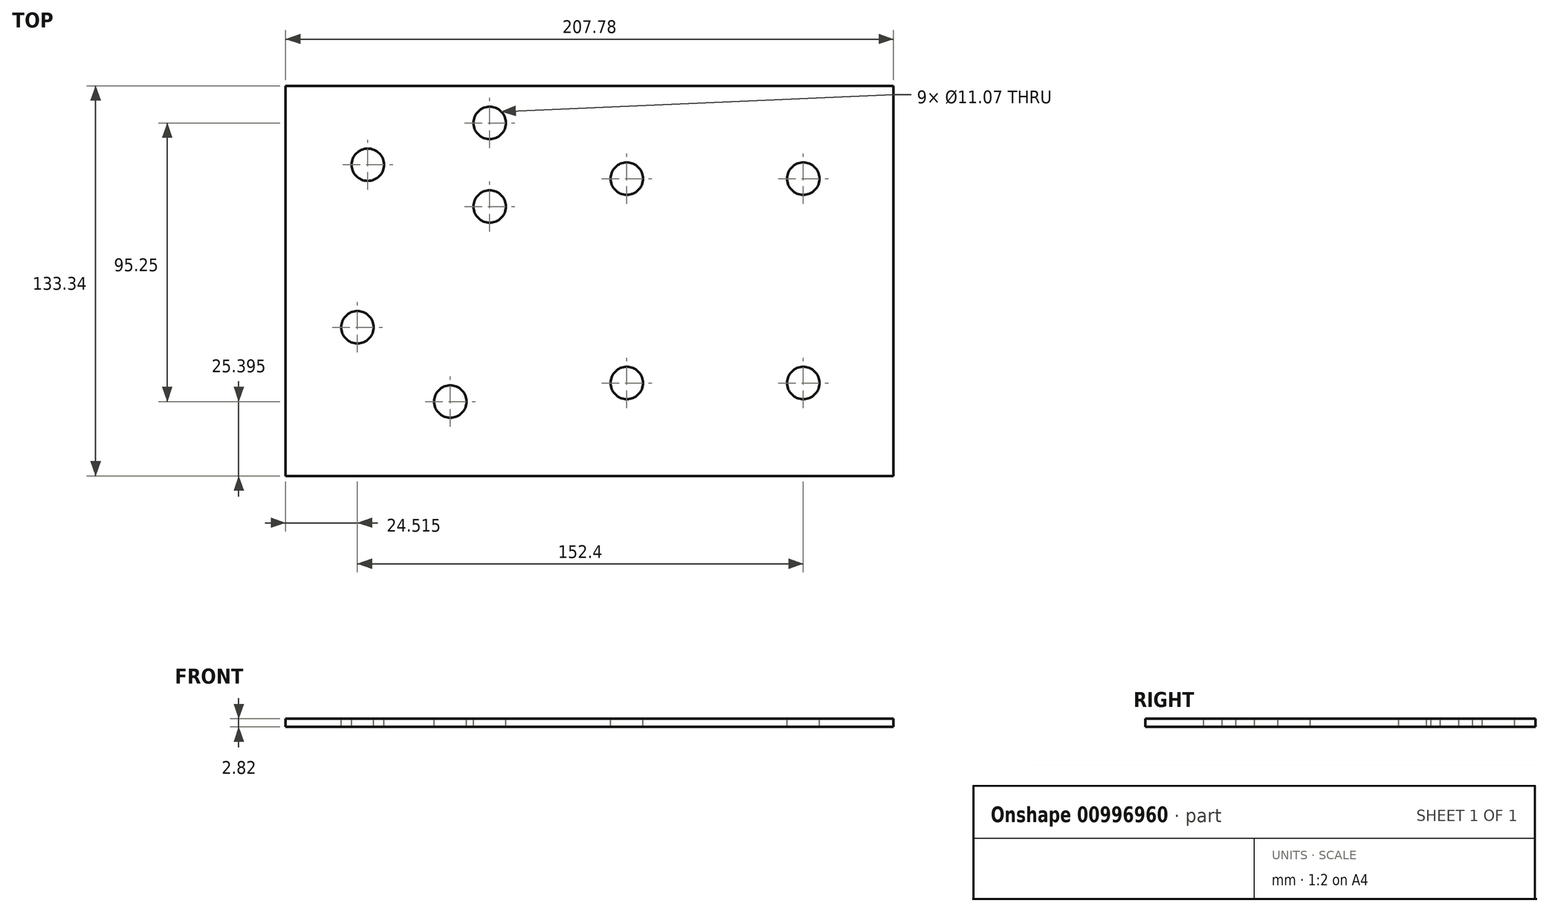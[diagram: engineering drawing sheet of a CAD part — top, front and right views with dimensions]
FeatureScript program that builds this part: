
annotation { "Feature Type Name" : "Feature", "Feature Type Description" : "" }
export const myFeature = defineFeature(function(context is Context, id is Id, definition is map)
    precondition{}
    {
        {
            var Q0;
            Q0=qCreatedBy(makeId("Top.planeOp"),FACE);
            var sketch = newSketch(context, id + "F0", { "sketchPlane" : qUnion([Q0])});
            skLineSegment(sketch, "E0.bottom", {"start": v(103.89, -66.67) * mm, "end": v(-103.89, -66.68) * mm});
            skLineSegment(sketch, "E0.top", {"start": v(103.89, 66.68) * mm, "end": v(-103.89, 66.67) * mm});
            skLineSegment(sketch, "E0.left", {"start": v(103.89, -66.67) * mm, "end": v(103.89, 66.68) * mm});
            skLineSegment(sketch, "E0.right", {"start": v(-103.89, -66.68) * mm, "end": v(-103.89, 66.68) * mm});
            skPoint(sketch, "E0.middle", {"position": v(0, 0) * mm});
            skSolve(sketch);
        }
        {
            var Q0;
            Q0=qSketchRegion(id+"F0",true);
            extrude(context, id + "F1", {"entities" : qUnion([Q0]), "depth" : 2.82 * mm, "offsetDistance" : 25.4 * mm});
        }
        {
            var Q0;
            Q0=makeQuery(id+"F1.opExtrude","CAP_FACE",FACE,{"disambiguationData":[OSD([sQuery(id+"F0.wireOp",EDGE,"E0.bottom"),sQuery(id+"F0.wireOp",EDGE,"E0.top"),sQuery(id+"F0.wireOp",EDGE,"E0.left"),sQuery(id+"F0.wireOp",EDGE,"E0.right")])],"isStart":false});
            var sketch = newSketch(context, id + "F2", { "sketchPlane" : qUnion([Q0])});
            skCircle(sketch, "E1", {"center": v(-75.82, 39.69) * mm, "radius": 5.54 * mm});
            skCircle(sketch, "E2", {"center": v(-79.38, -15.87) * mm, "radius": 5.54 * mm});
            skCircle(sketch, "E3", {"center": v(-34.16, 53.98) * mm, "radius": 5.54 * mm});
            skCircle(sketch, "E4", {"center": v(-34.16, 25.4) * mm, "radius": 5.54 * mm});
            skCircle(sketch, "E5", {"center": v(12.7, 34.93) * mm, "radius": 5.54 * mm});
            skCircle(sketch, "E6", {"center": v(-47.62, -41.28) * mm, "radius": 5.54 * mm});
            skCircle(sketch, "E7", {"center": v(73.02, 34.93) * mm, "radius": 5.54 * mm});
            skCircle(sketch, "E8", {"center": v(12.7, -34.92) * mm, "radius": 5.54 * mm});
            skCircle(sketch, "E9", {"center": v(73.03, -34.92) * mm, "radius": 5.54 * mm});
            skLineSegment(sketch, "E10", {"start": v(0, 66.68) * mm, "end": v(0, -66.68) * mm, "construction": true});
            skLineSegment(sketch, "E11", {"start": v(-103.89, 0) * mm, "end": v(103.89, 0) * mm, "construction": true});
            skLineSegment(sketch, "E12.bottom", {"start": v(100.71, -64.67) * mm, "end": v(-100.71, -64.67) * mm, "construction": true});
            skLineSegment(sketch, "E12.top", {"start": v(100.71, 64.67) * mm, "end": v(-100.71, 64.67) * mm, "construction": true});
            skLineSegment(sketch, "E12.left", {"start": v(100.71, -64.67) * mm, "end": v(100.71, 64.67) * mm, "construction": true});
            skLineSegment(sketch, "E12.right", {"start": v(-100.71, -64.67) * mm, "end": v(-100.71, 64.67) * mm, "construction": true});
            skPoint(sketch, "E12.middle", {"position": v(0, 0) * mm});
            skLineSegment(sketch, "E13", {"start": v(-21.46, 64.67) * mm, "end": v(-21.46, -64.67) * mm, "construction": true});
            skLineSegment(sketch, "E14", {"start": v(-46.86, 64.67) * mm, "end": v(-46.86, 0) * mm, "construction": true});
            skLineSegment(sketch, "E15", {"start": v(-50.04, 64.67) * mm, "end": v(-50.04, 0) * mm, "construction": true});
            skLineSegment(sketch, "E16", {"start": v(-103.89, 10.7) * mm, "end": v(103.89, 10.7) * mm, "construction": true});
            skLineSegment(sketch, "E17", {"start": v(-34.16, 53.98) * mm, "end": v(-34.16, 25.4) * mm, "construction": true});
            skPoint(sketch, "E18", {"position": v(-34.16, 39.69) * mm});
            skSolve(sketch);
        }
        {
            var Q0;
            Q0=qSketchRegion(id+"F2",true);
            extrude(context, id + "F3", {"entities" : qUnion([Q0]), "operationType" : NewBodyOperationType.REMOVE, "endBound" : BoundingType.THROUGH_ALL, "oppositeDirection" : true, "depth" : 25.4 * mm, "offsetDistance" : 25.4 * mm});
        }
    });
